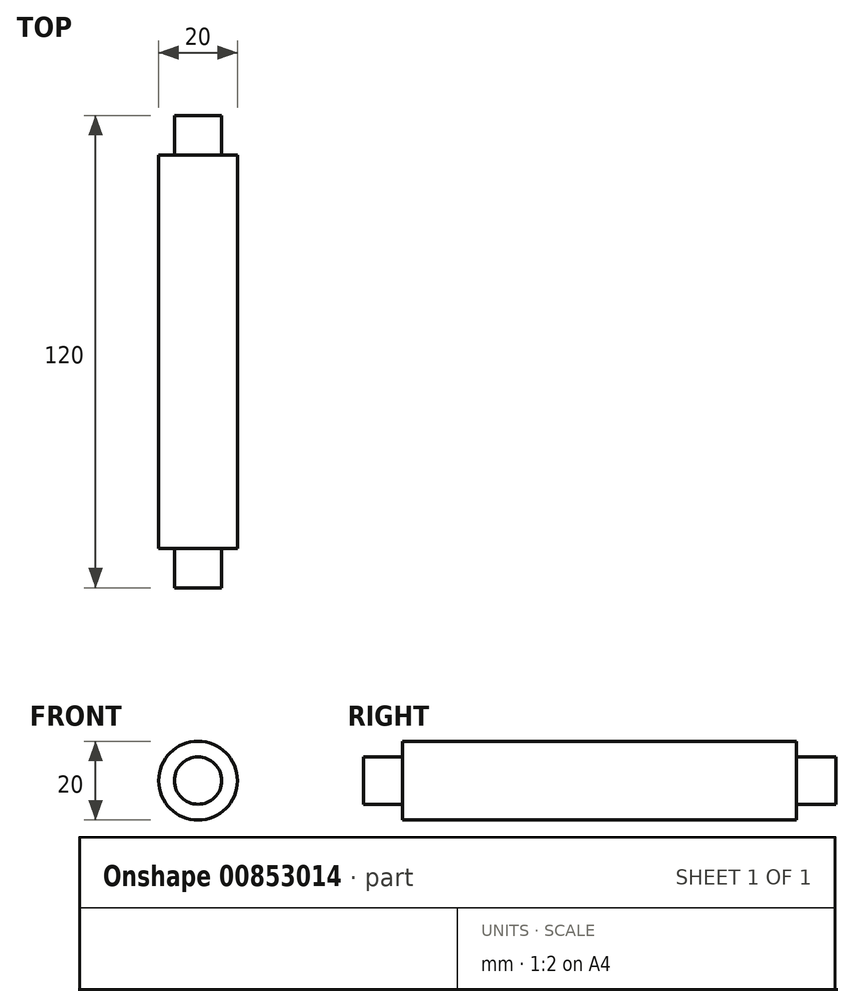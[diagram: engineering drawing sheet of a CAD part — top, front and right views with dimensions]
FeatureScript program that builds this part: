
annotation { "Feature Type Name" : "Feature", "Feature Type Description" : "" }
export const myFeature = defineFeature(function(context is Context, id is Id, definition is map)
    precondition{}
    {
        {
            var Q0;
            Q0=qCreatedBy(makeId("Top.planeOp"),FACE);
            var sketch = newSketch(context, id + "F0", { "sketchPlane" : qUnion([Q0])});
            skLineSegment(sketch, "E0", {"start": v(0, -60) * mm, "end": v(-6, -60) * mm});
            skLineSegment(sketch, "E1", {"start": v(-6, -60) * mm, "end": v(-6, -50) * mm});
            skLineSegment(sketch, "E2", {"start": v(-6, -50) * mm, "end": v(-10, -50) * mm});
            skLineSegment(sketch, "E3", {"start": v(-10, -50) * mm, "end": v(-10, 50) * mm});
            skLineSegment(sketch, "E4", {"start": v(-10, 50) * mm, "end": v(-6, 50) * mm});
            skLineSegment(sketch, "E5", {"start": v(-6, 50) * mm, "end": v(-6, 60) * mm});
            skLineSegment(sketch, "E6", {"start": v(-6, 60) * mm, "end": v(0, 60) * mm});
            skLineSegment(sketch, "E7", {"start": v(0, 60) * mm, "end": v(0, -60) * mm});
            skSolve(sketch);
        }
        {
            var Q0;
            Q0=makeQuery(id+"F0.imprint","IMPRINT",FACE,{"disambiguationData":[TD([[makeQuery(id+"F0.imprint","IMPRINT",EDGE,{"derivedFrom":sQuery(id+"F0.wireOp",EDGE,"E0")}),-1.0]])]});
            var Q1;
            Q1=sQuery(id+"F0.wireOp",EDGE,"E7");
            revolve(context, id + "F1", {"surfaceOperationType" : NewSurfaceOperationType.NEW, "entities" : qUnion([Q0]), "axis" : qUnion([Q1]), "revolveType" : RevolveType.FULL});
        }
    });
